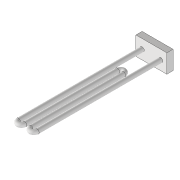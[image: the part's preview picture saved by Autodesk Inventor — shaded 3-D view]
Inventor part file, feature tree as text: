
AUTODESK INVENTOR PART (.ipt)
format: ipt  version: 2020 (Build 240168000, 168)  size: 121,344 bytes
history: native  units: mm
features: sketch x3, extrude x1, sweep x1
ambient origin geometry x8: Origin, YZ Plane, XZ Plane, XY Plane, X Axis, Y Axis, Z Axis, Center Point
bodies: Volumenkörper1 (feature_tree), Volumenkörper2 (feature_tree)
feature tree (5):
  extrude  "Extrusion1"  Depth=30.0mm
  sweep  "Sweeping1"
  sketch  "Skizze1"  dims[d0=50.0mm d1=30.0mm]
  sketch  "Skizze2"  dims[d2=10.0mm d3=0.0mm d4=7.0mm]
  sketch  "Skizze3"  dims[d5=7.0mm d6=30.0mm d7=30.0mm d8=15.0mm d9=200.0mm d10=200.0mm d11=150.0mm d12=10.0mm d13=10.0mm d14=0.0mm d15=0.0mm]
